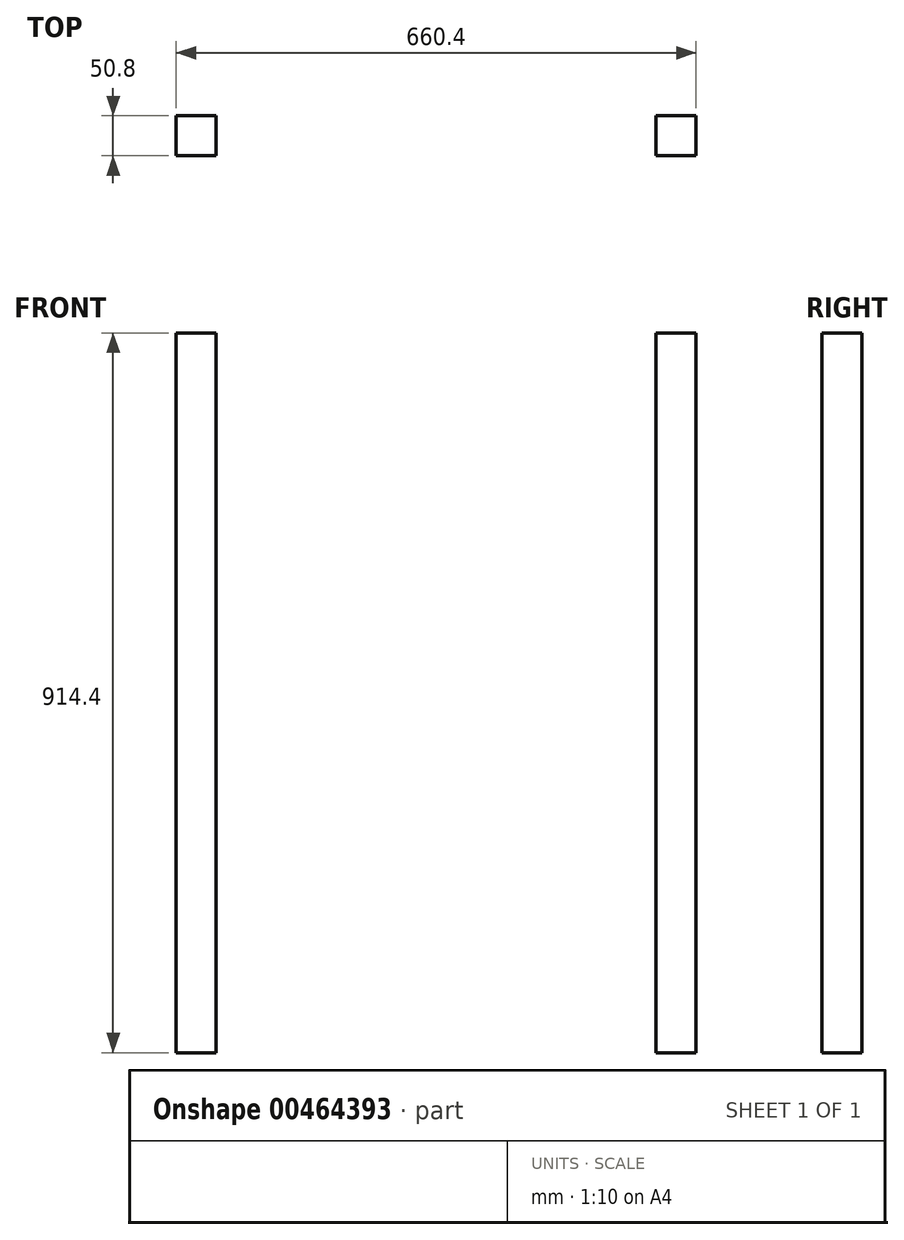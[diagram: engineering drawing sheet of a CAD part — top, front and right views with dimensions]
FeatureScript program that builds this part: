
annotation { "Feature Type Name" : "Feature", "Feature Type Description" : "" }
export const myFeature = defineFeature(function(context is Context, id is Id, definition is map)
    precondition{}
    {
        {
            var Q0;
            Q0=qCreatedBy(makeId("Top.planeOp"),FACE);
            var sketch = newSketch(context, id + "F0", { "sketchPlane" : qUnion([Q0])});
            skLineSegment(sketch, "E0.bottom", {"start": v(-25.4, 0) * mm, "end": v(25.4, 0) * mm});
            skLineSegment(sketch, "E0.top", {"start": v(-25.4, 50.8) * mm, "end": v(25.4, 50.8) * mm});
            skLineSegment(sketch, "E0.left", {"start": v(-25.4, 0) * mm, "end": v(-25.4, 50.8) * mm});
            skLineSegment(sketch, "E0.right", {"start": v(25.4, 0) * mm, "end": v(25.4, 50.8) * mm});
            skLineSegment(sketch, "E1.bottom", {"start": v(-635, 0) * mm, "end": v(-584.2, 0) * mm});
            skLineSegment(sketch, "E1.top", {"start": v(-635, 50.8) * mm, "end": v(-584.2, 50.8) * mm});
            skLineSegment(sketch, "E1.left", {"start": v(-635, 0) * mm, "end": v(-635, 50.8) * mm});
            skLineSegment(sketch, "E1.right", {"start": v(-584.2, 0) * mm, "end": v(-584.2, 50.8) * mm});
            skSolve(sketch);
        }
        {
            var Q0;
            Q0=makeQuery(id+"F0.imprint","IMPRINT",FACE,{"disambiguationData":[TD([[makeQuery(id+"F0.imprint","IMPRINT",EDGE,{"derivedFrom":sQuery(id+"F0.wireOp",EDGE,"E0.bottom")}),1.0]])]});
            var Q1;
            Q1=makeQuery(id+"F0.imprint","IMPRINT",FACE,{"disambiguationData":[TD([[makeQuery(id+"F0.imprint","IMPRINT",EDGE,{"derivedFrom":sQuery(id+"F0.wireOp",EDGE,"E1.bottom")}),1.0]])]});
            extrude(context, id + "F1", {"entities" : qUnion([Q0, Q1]), "endBound" : BoundingType.SYMMETRIC, "depth" : 914.4 * mm});
        }
    });
